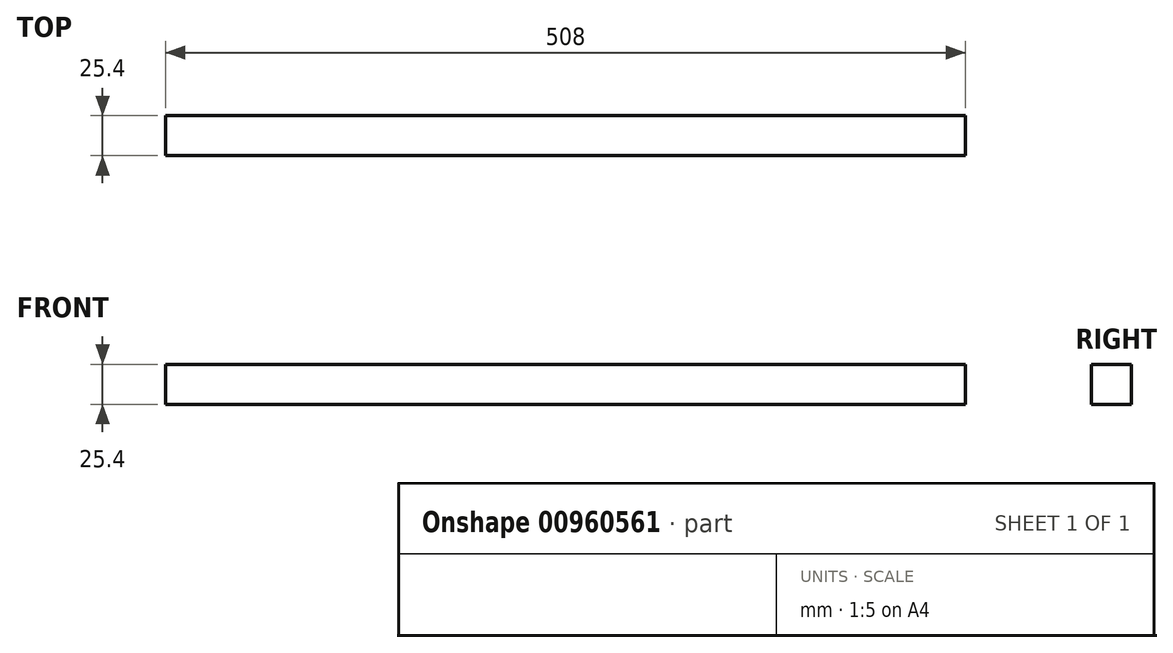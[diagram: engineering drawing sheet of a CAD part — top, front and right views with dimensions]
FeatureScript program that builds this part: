
annotation { "Feature Type Name" : "Feature", "Feature Type Description" : "" }
export const myFeature = defineFeature(function(context is Context, id is Id, definition is map)
    precondition{}
    {
        {
            var Q0;
            Q0=qCreatedBy(makeId("Front.planeOp"),FACE);
            var sketch = newSketch(context, id + "F0", { "sketchPlane" : qUnion([Q0])});
            skLineSegment(sketch, "E0.bottom", {"start": v(-204.17, -29.4) * mm, "end": v(303.83, -29.4) * mm});
            skLineSegment(sketch, "E0.top", {"start": v(-204.17, -54.8) * mm, "end": v(303.83, -54.8) * mm});
            skLineSegment(sketch, "E0.left", {"start": v(-204.17, -29.4) * mm, "end": v(-204.17, -54.8) * mm});
            skLineSegment(sketch, "E0.right", {"start": v(303.83, -29.4) * mm, "end": v(303.83, -54.8) * mm});
            skPoint(sketch, "E0.middle", {"position": v(49.83, -42.1) * mm});
            skSolve(sketch);
        }
        {
            var Q0;
            Q0 = qSketchRegion(id + "F0", true);
            extrude(context, id + "F1", {"entities" : qUnion([Q0]), "depth" : 25.4 * mm, "offsetDistance" : 25.4 * mm});
        }
    });
